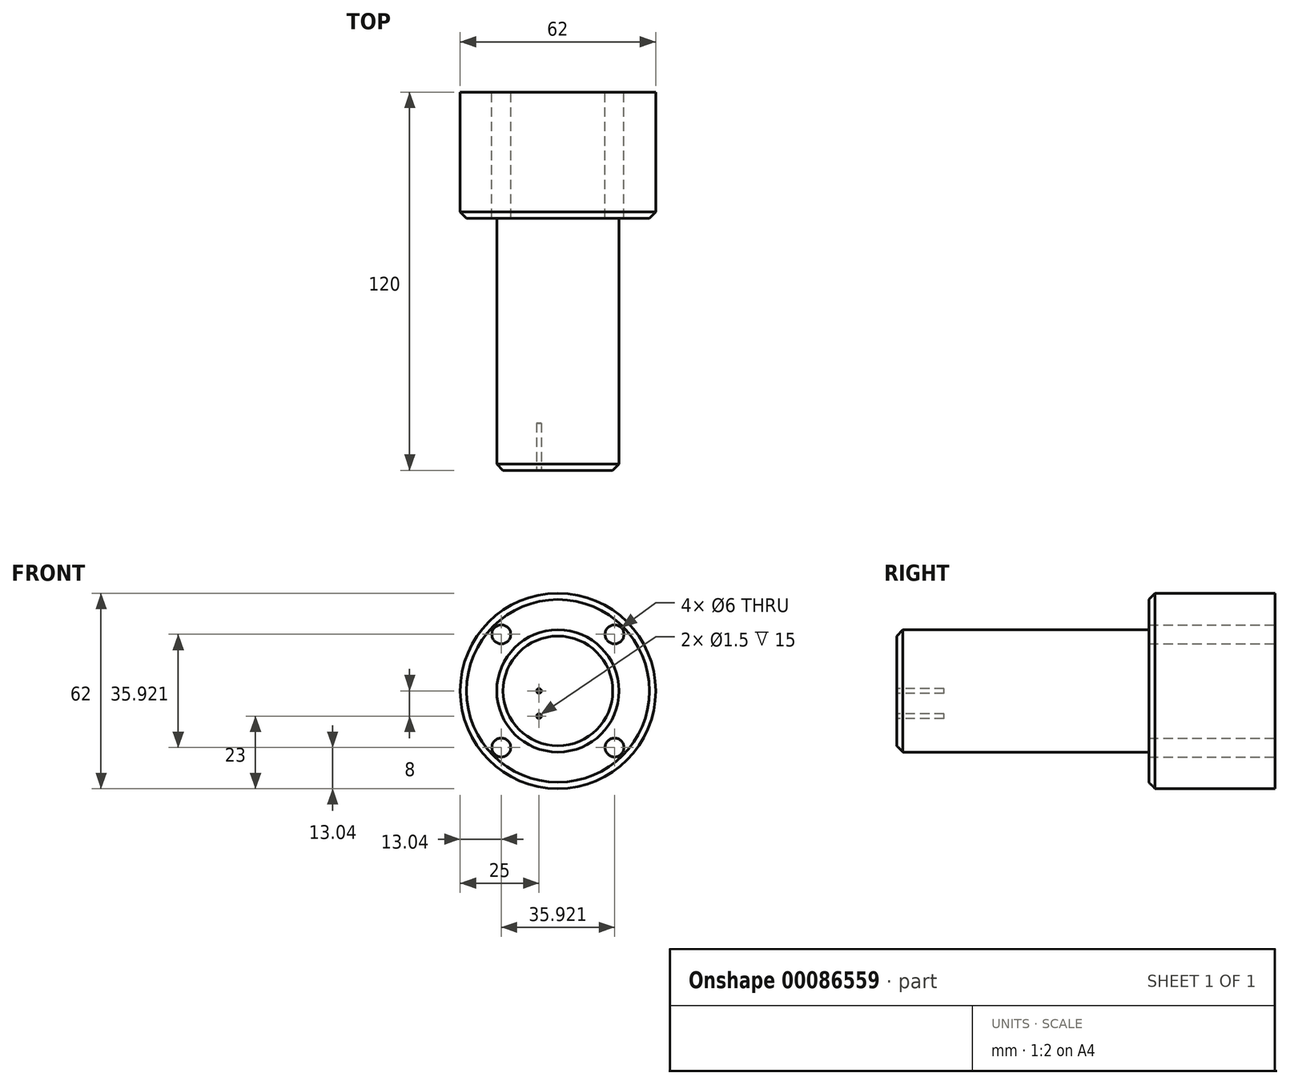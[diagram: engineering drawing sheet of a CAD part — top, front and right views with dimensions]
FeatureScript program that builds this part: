
annotation { "Feature Type Name" : "Feature", "Feature Type Description" : "" }
export const myFeature = defineFeature(function(context is Context, id is Id, definition is map)
    precondition{}
    {
        {
            var Q0;
            Q0=qCreatedBy(makeId("Front.planeOp"),FACE);
            var sketch = newSketch(context, id + "F0", { "sketchPlane" : qUnion([Q0])});
            skCircle(sketch, "E0", {"center": v(0, 0) * mm, "radius": 31 * mm});
            skCircle(sketch, "E1", {"center": v(0, 0) * mm, "radius": 25.4 * mm, "construction": true});
            skCircle(sketch, "E2", {"center": v(-17.96, 17.96) * mm, "radius": 3 * mm});
            skLineSegment(sketch, "E3", {"start": v(-17.96, 17.96) * mm, "end": v(0, 0) * mm, "construction": true});
            skLineSegment(sketch, "E4", {"start": v(0, 0) * mm, "end": v(0, 31) * mm, "construction": true});
            skCircle(sketch, "E5.1.0", {"center": v(-17.96, -17.96) * mm, "radius": 3 * mm});
            skCircle(sketch, "E5.2.0", {"center": v(17.96, -17.96) * mm, "radius": 3 * mm});
            skCircle(sketch, "E5.3.0", {"center": v(17.96, 17.96) * mm, "radius": 3 * mm});
            skSolve(sketch);
        }
        {
            var Q0;
            Q0 = qSketchRegion(id + "F0", true);
            extrude(context, id + "F1", {"entities" : qUnion([Q0]), "depth" : 40 * mm});
        }
        {
            var Q0;
            Q0=makeQuery(id+"F1.opExtrude","CAP_FACE",FACE,{"disambiguationData":[OSD([sQuery(id+"F0.wireOp",EDGE,"E0"),sQuery(id+"F0.wireOp",EDGE,"E2"),sQuery(id+"F0.wireOp",EDGE,"E5.1.0"),sQuery(id+"F0.wireOp",EDGE,"E5.2.0"),sQuery(id+"F0.wireOp",EDGE,"E5.3.0")])],"isStart":false});
            var sketch = newSketch(context, id + "F2", { "sketchPlane" : qUnion([Q0])});
            skCircle(sketch, "E6.0.0", {"center": v(0, 0) * mm, "radius": 31 * mm});
            skCircle(sketch, "E7", {"center": v(0, 0) * mm, "radius": 19.4 * mm});
            skCircle(sketch, "E8.0", {"center": v(-17.96, 17.96) * mm, "radius": 3 * mm});
            skCircle(sketch, "E9", {"center": v(-17.96, 17.96) * mm, "radius": 6 * mm});
            skSolve(sketch);
        }
        {
            var Q0;
            Q0=makeQuery(id+"F2.imprint","IMPRINT",FACE,{"disambiguationData":[TD([[makeQuery(id+"F2.imprint","IMPRINT",EDGE,{"derivedFrom":sQuery(id+"F2.wireOp",EDGE,"E7")}),1.0]])]});
            extrude(context, id + "F3", {"entities" : qUnion([Q0]), "operationType" : NewBodyOperationType.ADD, "depth" : 80 * mm});
        }
        {
            var Q0;
            Q0=makeQuery(id+"F3.opExtrude","CAP_FACE",FACE,{"disambiguationData":[OSD([sQuery(id+"F2.wireOp",EDGE,"E7")])],"isStart":false});
            var sketch = newSketch(context, id + "F4", { "sketchPlane" : qUnion([Q0])});
            skCircle(sketch, "E10.0", {"center": v(0, 0) * mm, "radius": 19.4 * mm});
            skLineSegment(sketch, "E11", {"start": v(0, 19.4) * mm, "end": v(0, -19.4) * mm, "construction": true});
            skCircle(sketch, "E12", {"center": v(-6, 0) * mm, "radius": 0.75 * mm});
            skCircle(sketch, "E13", {"center": v(-6, -8) * mm, "radius": 0.75 * mm});
            skLineSegment(sketch, "E14", {"start": v(-6, -8) * mm, "end": v(-6, 0) * mm, "construction": true});
            skSolve(sketch);
        }
        {
            var Q0;
            Q0=makeQuery(id+"F4.imprint","IMPRINT",FACE,{"disambiguationData":[TD([[makeQuery(id+"F4.imprint","IMPRINT",EDGE,{"derivedFrom":sQuery(id+"F4.wireOp",EDGE,"E12")}),1.0]])]});
            var Q1;
            Q1=makeQuery(id+"F4.imprint","IMPRINT",FACE,{"disambiguationData":[TD([[makeQuery(id+"F4.imprint","IMPRINT",EDGE,{"derivedFrom":sQuery(id+"F4.wireOp",EDGE,"E13")}),1.0]])]});
            extrude(context, id + "F5", {"entities" : qUnion([Q0, Q1]), "operationType" : NewBodyOperationType.REMOVE, "oppositeDirection" : true, "depth" : 15 * mm});
        }
        {
            var Q0;
            Q0=makeQuery(id+"F3.opExtrude","CAP_EDGE",EDGE,{"disambiguationData":[OSD([sQuery(id+"F2.wireOp",EDGE,"E7")])],"isStart":false});
            var Q1;
            Q1=makeQuery(id+"F1.opExtrude","CAP_EDGE",EDGE,{"disambiguationData":[OSD([sQuery(id+"F0.wireOp",EDGE,"E0")])],"isStart":false});
            chamfer(context, id + "F6", {"entities" : qUnion([Q0, Q1]), "width" : 2 * mm, "tangentPropagation" : true});
        }
    });
